# Revit family: R1208-HF
name_source: partatom
category: Plumbing Fixtures
units: mm (PartAtom-declared; Revit-internal decimal feet)

## family parameters
Always vertical = Yes
Cut with Voids When Loaded = No
Enable Cutting in Views = No
Maintain Annotation Orientation = No
OmniClass Number = 23.45.00.00
OmniClass Title = Sanitary, Laundry, and Cleaning Equipment
Part Type = Normal
Room Calculation Point = No
Round Connector Dimension = Use Diameter
Shared = No
Work Plane-Based = No

## types (4) — shared parameters
Default Elevation = 0' - 0"
R = 0' - 2 7/8"
Y = 0' - 7"

## per-type parameters (varying)
| type | A | B | C | D | PIPE SIZE |
| R1203-HF | 1' - 4" | 1' - 1" | 0' - 7" | 1' - 0 3/4" | 0' - 3 11/32" |
| R1204-HF | 1' - 4" | 1' - 1 1/16" | 0' - 7" | 1' - 0 3/4" | 0' - 4 3/8" |
| R1206-HF | 1' - 8" | 1' - 3 21/32" | 0' - 7 1/2" | 1' - 1" | 0' - 6 5/16" |
| R1208-HF | 1' - 8" | 1' - 3 21/32" | 0' - 7 1/2" | 1' - 1" | 0' - 8 3/8" |

## geometry (parser evidence)
native form markers: Sweep x2
no freeform markers — native parametric forms only
